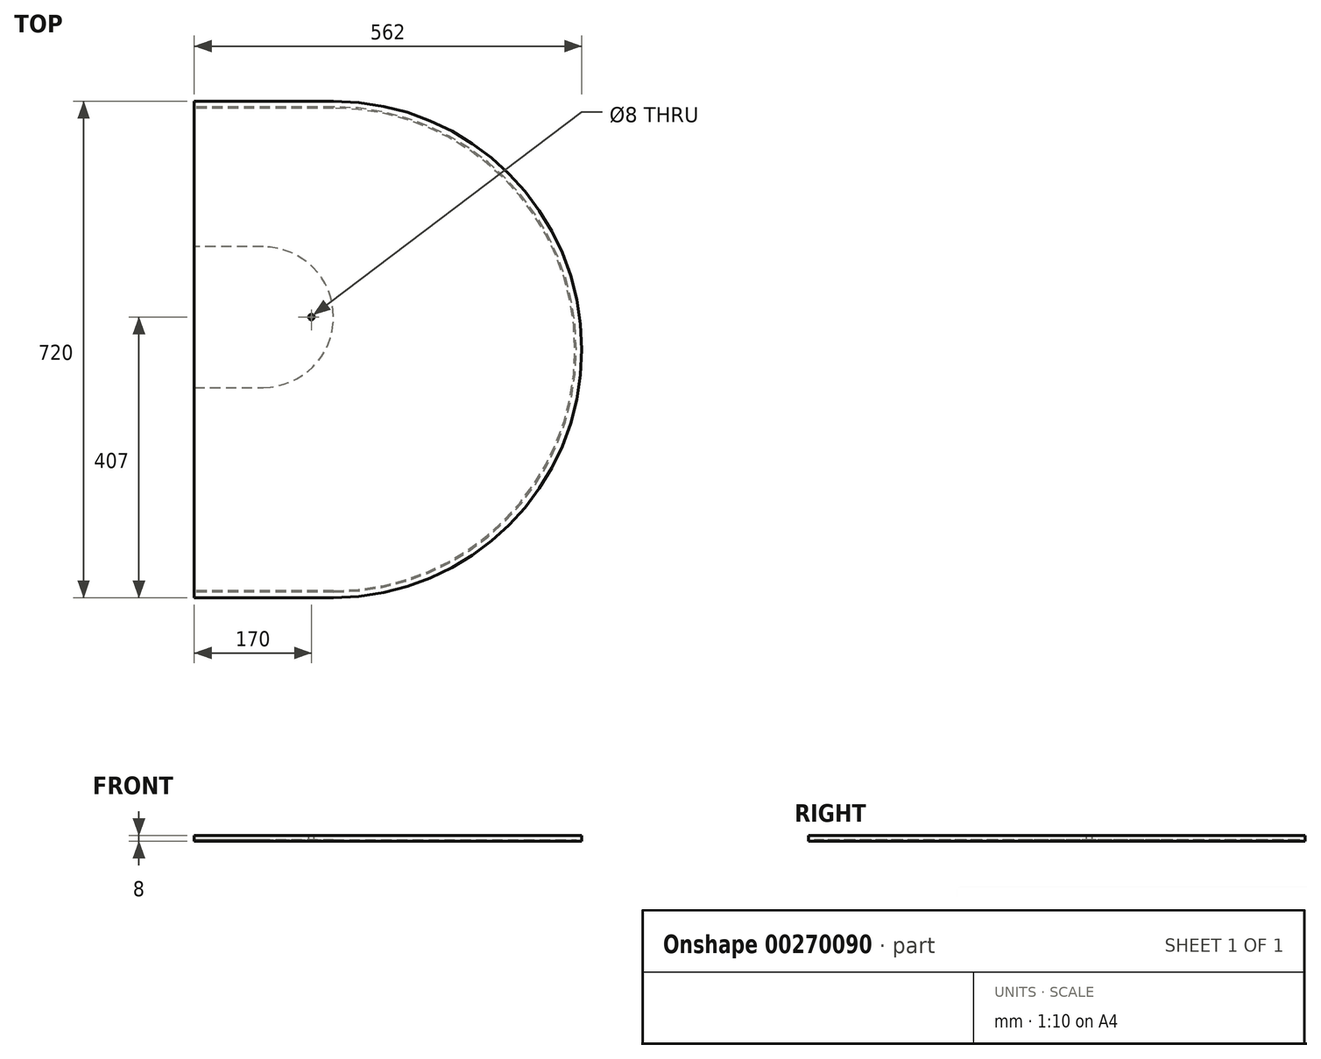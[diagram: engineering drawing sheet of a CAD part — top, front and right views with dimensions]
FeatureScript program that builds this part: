
annotation { "Feature Type Name" : "Feature", "Feature Type Description" : "" }
export const myFeature = defineFeature(function(context is Context, id is Id, definition is map)
    precondition{}
    {
        {
            var Q0;
            Q0=qCreatedBy(makeId("Top.planeOp"),FACE);
            var sketch = newSketch(context, id + "F0", { "sketchPlane" : qUnion([Q0])});
            skArc(sketch, "E0", {"start": v(0, -360) * mm, "mid": v(360, 0) * mm, "end": v(0, 360) * mm});
            skLineSegment(sketch, "E1.bottom", {"start": v(0, 360) * mm, "end": v(-102, 360) * mm});
            skLineSegment(sketch, "E1.top", {"start": v(0, -360) * mm, "end": v(-102, -360) * mm});
            skLineSegment(sketch, "E1.right", {"start": v(-102, 360) * mm, "end": v(-102, 360) * mm});
            skLineSegment(sketch, "E2.bottom", {"start": v(-102, -360) * mm, "end": v(-202, -360) * mm});
            skLineSegment(sketch, "E2.top", {"start": v(-102, 360) * mm, "end": v(-202, 360) * mm});
            skLineSegment(sketch, "E2.right", {"start": v(-202, -360) * mm, "end": v(-202, 360) * mm});
            skSolve(sketch);
        }
        {
            var Q0;
            Q0=makeQuery(id+"F0.imprint","IMPRINT",FACE,{"disambiguationData":[TD([[makeQuery(id+"F0.imprint","IMPRINT",EDGE,{"derivedFrom":sQuery(id+"F0.wireOp",EDGE,"E0")}),1.0]])]});
            extrude(context, id + "F1", {"entities" : qUnion([Q0]), "depth" : 8 * mm});
        }
        {
            var Q0;
            Q0=makeQuery(id+"F1.opExtrude","CAP_FACE",FACE,{"disambiguationData":[OSD([sQuery(id+"F0.wireOp",EDGE,"E0"),sQuery(id+"F0.wireOp",EDGE,"E1.bottom"),sQuery(id+"F0.wireOp",EDGE,"E1.top"),sQuery(id+"F0.wireOp",EDGE,"E1.right")])],"isStart":true});
            var sketch = newSketch(context, id + "F2", { "sketchPlane" : qUnion([Q0])});
            skArc(sketch, "E3", {"start": v(0, -350) * mm, "mid": v(350, 0) * mm, "end": v(0, 350) * mm});
            skArc(sketch, "E4.0", {"start": v(0, -352) * mm, "mid": v(352, 0) * mm, "end": v(0, 352) * mm});
            skLineSegment(sketch, "E5", {"start": v(0, -350) * mm, "end": v(0, 350) * mm});
            skPoint(sketch, "E6.orphan", {"position": v(0, -431.73) * mm});
            skLineSegment(sketch, "E7", {"start": v(0, -352) * mm, "end": v(-202, -352) * mm});
            skLineSegment(sketch, "E8", {"start": v(0, -350) * mm, "end": v(-202, -350) * mm});
            skLineSegment(sketch, "E9", {"start": v(0, 350) * mm, "end": v(-202, 350) * mm});
            skLineSegment(sketch, "E10", {"start": v(0, 352) * mm, "end": v(-202, 352) * mm});
            skSolve(sketch);
        }
        {
            var Q0;
            Q0=makeQuery(id+"F2.imprint","IMPRINT",FACE,{"disambiguationData":[TD([[makeQuery(id+"F2.imprint","IMPRINT",EDGE,{"derivedFrom":sQuery(id+"F2.wireOp",EDGE,"E3")}),-1.0]])]});
            extrude(context, id + "F3", {"entities" : qUnion([Q0]), "operationType" : NewBodyOperationType.REMOVE, "oppositeDirection" : true, "depth" : 2 * mm});
        }
        {
            var Q0;
            Q0=makeQuery(id+"F1.opExtrude","CAP_FACE",FACE,{"disambiguationData":[OSD([sQuery(id+"F0.wireOp",EDGE,"E0"),sQuery(id+"F0.wireOp",EDGE,"E1.bottom"),sQuery(id+"F0.wireOp",EDGE,"E1.top"),sQuery(id+"F0.wireOp",EDGE,"E1.right")])],"isStart":false});
            var sketch = newSketch(context, id + "F4", { "sketchPlane" : qUnion([Q0])});
            skCircle(sketch, "E11", {"center": v(-32, 47) * mm, "radius": 4 * mm});
            skLineSegment(sketch, "E12", {"start": v(88.3, -55) * mm, "end": v(-730.48, -55) * mm, "construction": true});
            skArc(sketch, "E13", {"start": v(-102, -55) * mm, "mid": v(0, 47) * mm, "end": v(-102, 149) * mm});
            skLineSegment(sketch, "E14", {"start": v(-102, 149) * mm, "end": v(-202, 149) * mm});
            skLineSegment(sketch, "E15", {"start": v(-102, -55) * mm, "end": v(-202, -55) * mm});
            skLineSegment(sketch, "E16", {"start": v(-202, -55) * mm, "end": v(-202, 149) * mm});
            skSolve(sketch);
        }
        {
            var Q0;
            Q0=makeQuery(id+"F4.imprint","IMPRINT",FACE,{"disambiguationData":[TD([[makeQuery(id+"F4.imprint","IMPRINT",EDGE,{"derivedFrom":sQuery(id+"F4.wireOp",EDGE,"E11")}),1.0]])]});
            extrude(context, id + "F5", {"entities" : qUnion([Q0]), "operationType" : NewBodyOperationType.REMOVE, "endBound" : BoundingType.UP_TO_NEXT, "oppositeDirection" : true, "depth" : 25 * mm});
        }
        {
            var Q0;
            Q0=makeQuery(id+"F2.imprint","IMPRINT",FACE,{"disambiguationData":[TD([[makeQuery(id+"F2.imprint","IMPRINT",EDGE,{"derivedFrom":sQuery(id+"F2.wireOp",EDGE,"E5")}),1.0]])]});
            var sketch = newSketch(context, id + "F6", { "sketchPlane" : qUnion([Q0])});
            skLineSegment(sketch, "E17", {"start": v(-441.54, 55) * mm, "end": v(132.37, 55) * mm, "construction": true});
            skArc(sketch, "E18", {"start": v(-102, -149) * mm, "mid": v(0, -47) * mm, "end": v(-102, 55) * mm});
            skLineSegment(sketch, "E19", {"start": v(-102, -149) * mm, "end": v(-202, -149) * mm});
            skLineSegment(sketch, "E20", {"start": v(-202, -149) * mm, "end": v(-202, 55) * mm});
            skLineSegment(sketch, "E21", {"start": v(-202, 55) * mm, "end": v(-102, 55) * mm});
            skSolve(sketch);
        }
        {
            var Q0;
            Q0=makeQuery(id+"F6.imprint","IMPRINT",FACE,{"disambiguationData":[TD([[makeQuery(id+"F6.imprint","IMPRINT",EDGE,{"derivedFrom":sQuery(id+"F6.wireOp",EDGE,"E18")}),1.0]])]});
            var Q1;
            {var subQ0=sQuery(id+"F6.wireOp",EDGE,"E18");var subQ1=makeQuery(id+"F2.imprint","IMPRINT",EDGE,{"derivedFrom":sQuery(id+"F2.wireOp",EDGE,"E5")});var subQ2=makeQuery(id+"F6.imprint","INTERSECT",VERTEX,{"disambiguationData":[OD(0.0)],"derivedFrom":[subQ1,subQ0]});Q1=makeQuery(id+"F6.imprint","IMPRINT",FACE,{"disambiguationData":[TD([[makeQuery(id+"F6.imprint","IMPRINT",EDGE,{"disambiguationData":[TD([[subQ2,-1.0]])],"derivedFrom":subQ0}),1.0]])]});}
            extrude(context, id + "F7", {"entities" : qUnion([Q0, Q1]), "operationType" : NewBodyOperationType.REMOVE, "oppositeDirection" : true, "depth" : 2 * mm});
        }
    });
